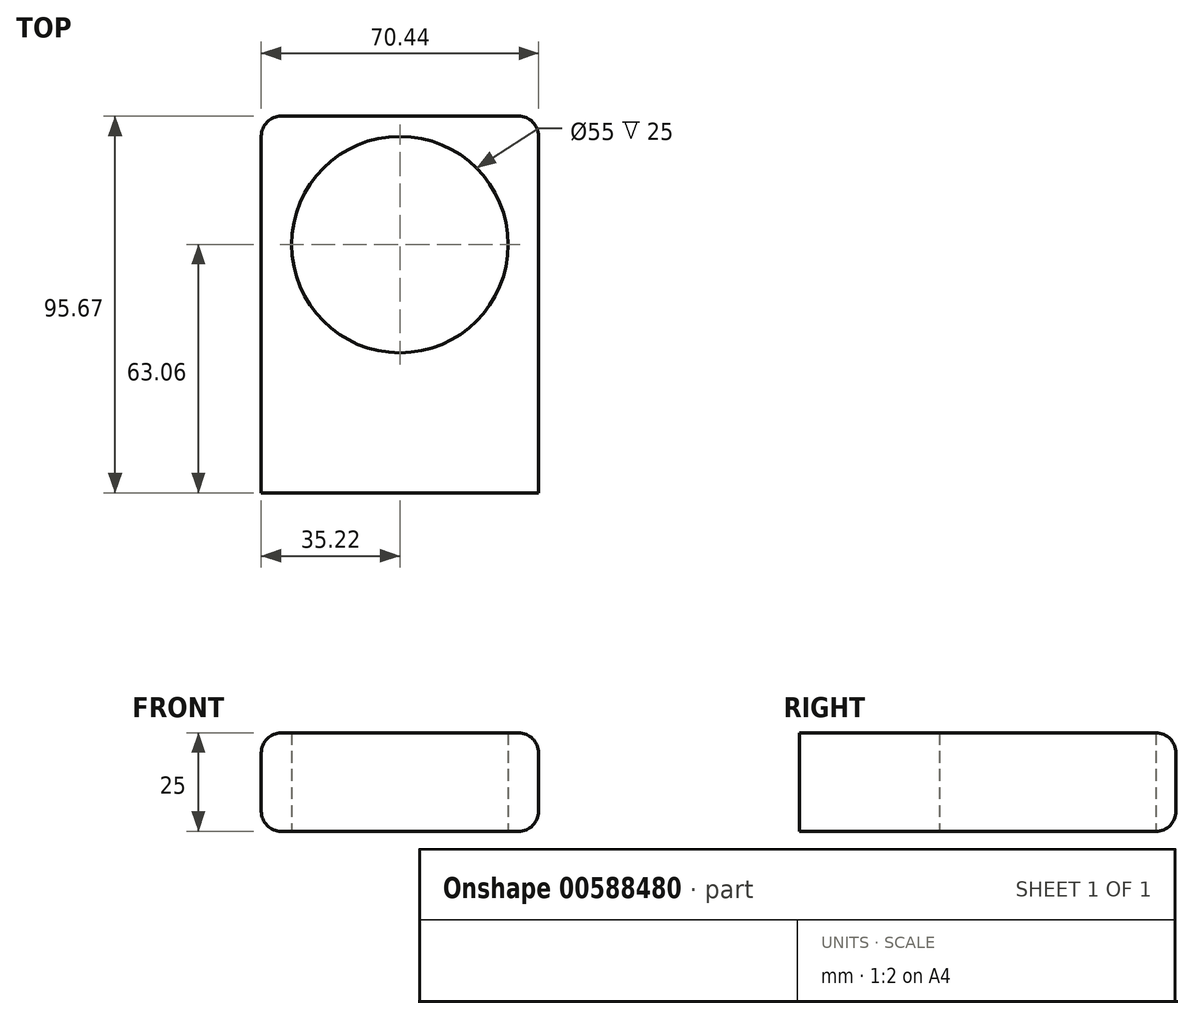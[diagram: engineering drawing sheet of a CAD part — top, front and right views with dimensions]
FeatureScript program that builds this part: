
annotation { "Feature Type Name" : "Feature", "Feature Type Description" : "" }
export const myFeature = defineFeature(function(context is Context, id is Id, definition is map)
    precondition{}
    {
        {
            var Q0;
            Q0=qCreatedBy(makeId("Top.planeOp"),FACE);
            var sketch = newSketch(context, id + "F0", { "sketchPlane" : qUnion([Q0])});
            skCircle(sketch, "E0", {"center": v(0, 0) * mm, "radius": 27.5 * mm});
            skLineSegment(sketch, "E1.bottom", {"start": v(-35.22, 32.6) * mm, "end": v(35.22, 32.6) * mm});
            skLineSegment(sketch, "E1.top", {"start": v(-35.22, -63.06) * mm, "end": v(35.22, -63.06) * mm});
            skLineSegment(sketch, "E1.left", {"start": v(-35.22, 32.6) * mm, "end": v(-35.22, -63.06) * mm});
            skLineSegment(sketch, "E1.right", {"start": v(35.22, 32.6) * mm, "end": v(35.22, -63.06) * mm});
            skSolve(sketch);
        }
        {
            var Q0;
            Q0=makeQuery(id+"F0.imprint","IMPRINT",FACE,{"disambiguationData":[TD([[makeQuery(id+"F0.imprint","IMPRINT",EDGE,{"derivedFrom":sQuery(id+"F0.wireOp",EDGE,"E0")}),-1.0]])]});
            extrude(context, id + "F1", {"entities" : qUnion([Q0]), "depth" : 25 * mm, "offsetDistance" : 25.4 * mm});
        }
        {
            var Q0;
            Q0=makeQuery(id+"F1.opExtrude","CAP_EDGE",EDGE,{"disambiguationData":[OSD([sQuery(id+"F0.wireOp",EDGE,"E1.right")])],"isStart":false});
            var Q1;
            Q1=makeQuery(id+"F1.opExtrude","CAP_EDGE",EDGE,{"disambiguationData":[OSD([sQuery(id+"F0.wireOp",EDGE,"E1.right")])],"isStart":true});
            var Q2;
            Q2=makeQuery(id+"F1.opExtrude","CAP_EDGE",EDGE,{"disambiguationData":[OSD([sQuery(id+"F0.wireOp",EDGE,"E1.left")])],"isStart":false});
            var Q3;
            Q3=makeQuery(id+"F1.opExtrude","CAP_EDGE",EDGE,{"disambiguationData":[OSD([sQuery(id+"F0.wireOp",EDGE,"E1.left")])],"isStart":true});
            var Q4;
            Q4=makeQuery(id+"F1.opExtrude","SWEPT_EDGE",EDGE,{"disambiguationData":[OSD([sQuery(id+"F0.wireOp",EDGE,"E1.bottom"),sQuery(id+"F0.wireOp",EDGE,"E1.left")])]});
            var Q5;
            Q5=makeQuery(id+"F1.opExtrude","SWEPT_EDGE",EDGE,{"disambiguationData":[OSD([sQuery(id+"F0.wireOp",EDGE,"E1.bottom"),sQuery(id+"F0.wireOp",EDGE,"E1.right")])]});
            var Q6;
            Q6=makeQuery(id+"F1.opExtrude","CAP_EDGE",EDGE,{"disambiguationData":[OSD([sQuery(id+"F0.wireOp",EDGE,"E1.bottom")])],"isStart":false});
            var Q7;
            Q7=makeQuery(id+"F1.opExtrude","CAP_EDGE",EDGE,{"disambiguationData":[OSD([sQuery(id+"F0.wireOp",EDGE,"E1.bottom")])],"isStart":true});
            fillet(context, id + "F2", {"entities" : qUnion([Q0, Q1, Q2, Q3, Q4, Q5, Q6, Q7]), "radius" : 5.08 * mm, "tangentPropagation" : true, "allowEdgeOverflow" : false});
        }
    });
